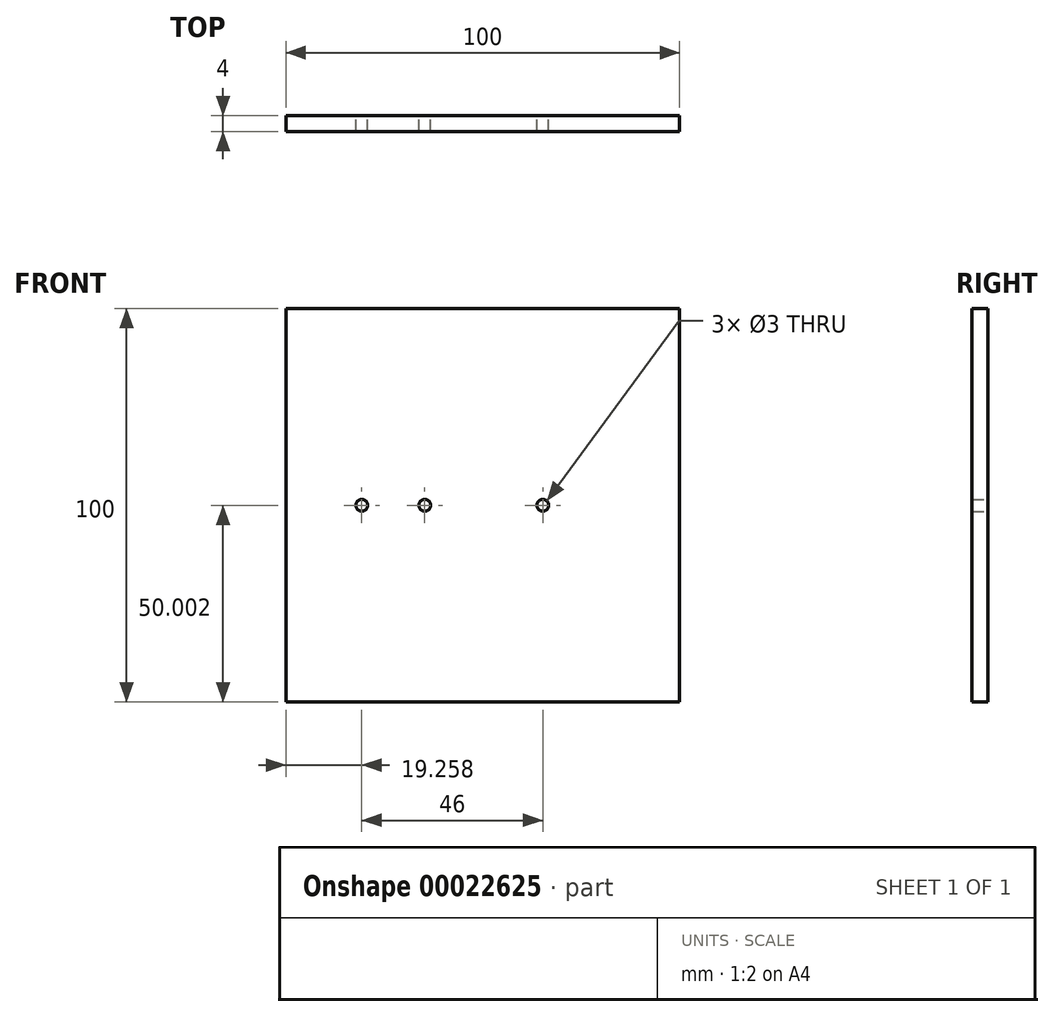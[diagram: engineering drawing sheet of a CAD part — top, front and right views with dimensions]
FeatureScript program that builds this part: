
annotation { "Feature Type Name" : "Feature", "Feature Type Description" : "" }
export const myFeature = defineFeature(function(context is Context, id is Id, definition is map)
    precondition{}
    {
        {
            var Q0;
            Q0=qCreatedBy(makeId("Front.planeOp"),FACE);
            var sketch = newSketch(context, id + "F0", { "sketchPlane" : qUnion([Q0])});
            skLineSegment(sketch, "E0.bottom", {"start": v(-59.03, -21.38) * mm, "end": v(40.97, -21.38) * mm});
            skLineSegment(sketch, "E0.top", {"start": v(-59.03, 78.62) * mm, "end": v(40.97, 78.62) * mm});
            skLineSegment(sketch, "E0.left", {"start": v(-59.03, -21.38) * mm, "end": v(-59.03, 78.62) * mm});
            skLineSegment(sketch, "E0.right", {"start": v(40.97, -21.38) * mm, "end": v(40.97, 78.62) * mm});
            skCircle(sketch, "E1", {"center": v(-39.77, 28.62) * mm, "radius": 1.5 * mm});
            skCircle(sketch, "E2", {"center": v(-23.77, 28.62) * mm, "radius": 1.5 * mm});
            skCircle(sketch, "E3", {"center": v(6.23, 28.62) * mm, "radius": 1.5 * mm});
            skPoint(sketch, "E4.orphan", {"position": v(-59.03, 28.62) * mm});
            skPoint(sketch, "E5.end.orphan", {"position": v(40.97, 28.62) * mm});
            skSolve(sketch);
        }
        {
            var Q0;
            Q0=makeQuery(id+"F0.imprint","IMPRINT",FACE,{"disambiguationData":[TD([[makeQuery(id+"F0.imprint","IMPRINT",EDGE,{"derivedFrom":sQuery(id+"F0.wireOp",EDGE,"E0.bottom")}),1.0]])]});
            extrude(context, id + "F1", {"entities" : qUnion([Q0]), "depth" : 4 * mm});
        }
    });
